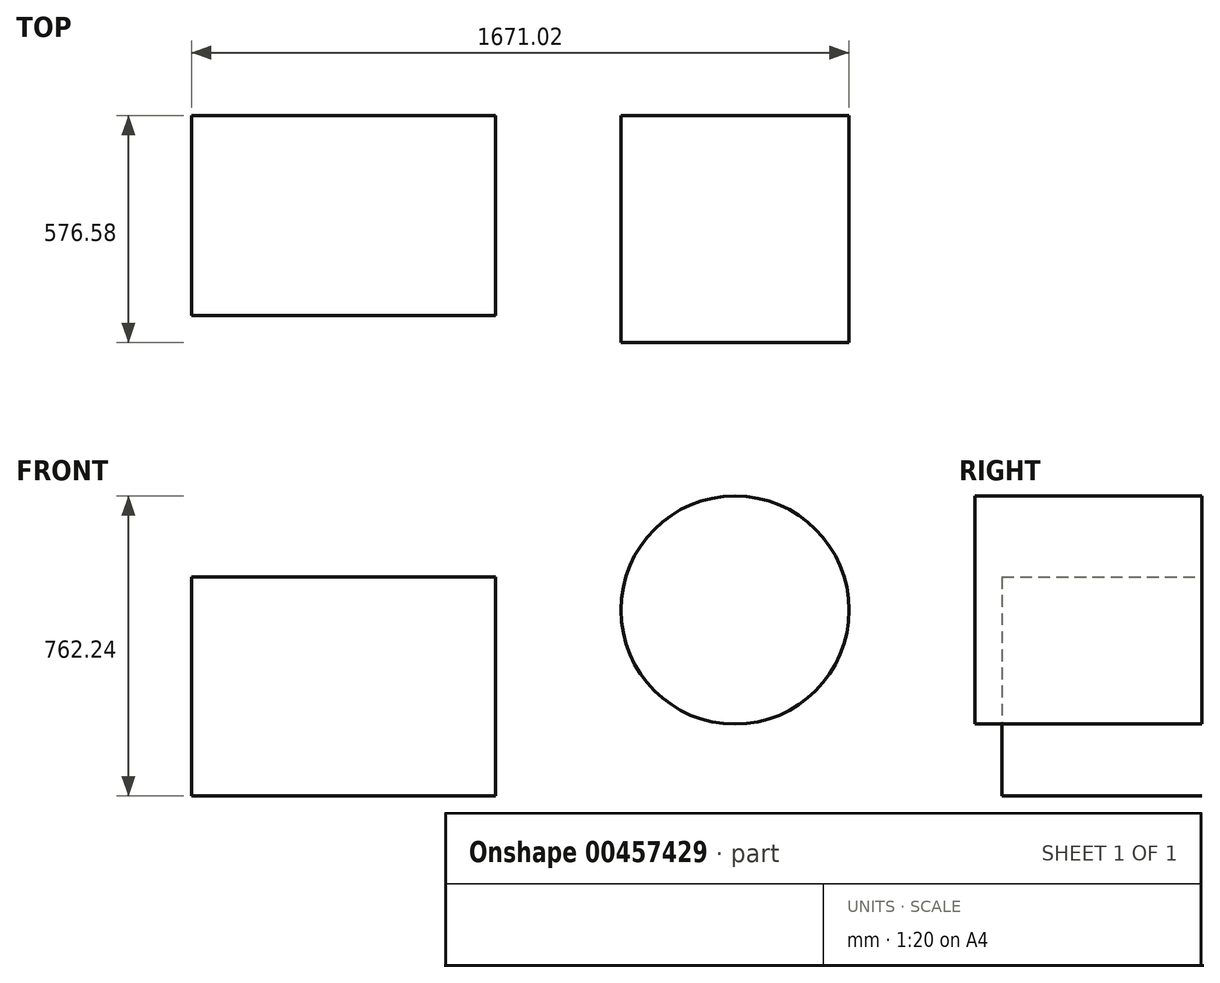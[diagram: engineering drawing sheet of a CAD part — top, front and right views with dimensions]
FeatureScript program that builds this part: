
annotation { "Feature Type Name" : "Feature", "Feature Type Description" : "" }
export const myFeature = defineFeature(function(context is Context, id is Id, definition is map)
    precondition{}
    {
        {
            var Q0;
            Q0=qCreatedBy(makeId("Front.planeOp"),FACE);
            var sketch = newSketch(context, id + "F0", { "sketchPlane" : qUnion([Q0])});
            skLineSegment(sketch, "E0.bottom", {"start": v(-310.88, 234.1) * mm, "end": v(462.3, 234.1) * mm});
            skLineSegment(sketch, "E0.top", {"start": v(-310.88, -322.17) * mm, "end": v(462.3, -322.17) * mm});
            skLineSegment(sketch, "E0.left", {"start": v(-310.88, 234.1) * mm, "end": v(-310.88, -322.17) * mm});
            skLineSegment(sketch, "E0.right", {"start": v(462.3, 234.1) * mm, "end": v(462.3, -322.17) * mm});
            skSolve(sketch);
        }
        {
            var Q0;
            Q0=makeQuery(id+"F0.imprint","IMPRINT",FACE,{"disambiguationData":[TD([[makeQuery(id+"F0.imprint","IMPRINT",EDGE,{"derivedFrom":sQuery(id+"F0.wireOp",EDGE,"E0.bottom")}),-1.0]])]});
            extrude(context, id + "F1", {"entities" : qUnion([Q0]), "depth" : 508 * mm, "offsetDistance" : 25.4 * mm});
        }
        {
            var Q0;
            Q0=qCreatedBy(makeId("Front.planeOp"),FACE);
            var sketch = newSketch(context, id + "F2", { "sketchPlane" : qUnion([Q0])});
            skCircle(sketch, "E1", {"center": v(1070.28, 150.22) * mm, "radius": 289.85 * mm});
            skSolve(sketch);
        }
        {
            var Q0;
            Q0=makeQuery(id+"F2.imprint","IMPRINT",FACE,{"disambiguationData":[TD([[makeQuery(id+"F2.imprint","IMPRINT",EDGE,{"derivedFrom":sQuery(id+"F2.wireOp",EDGE,"E1")}),1.0]])]});
            extrude(context, id + "F3", {"entities" : qUnion([Q0]), "depth" : 576.58 * mm, "offsetDistance" : 25.4 * mm});
        }
    });
